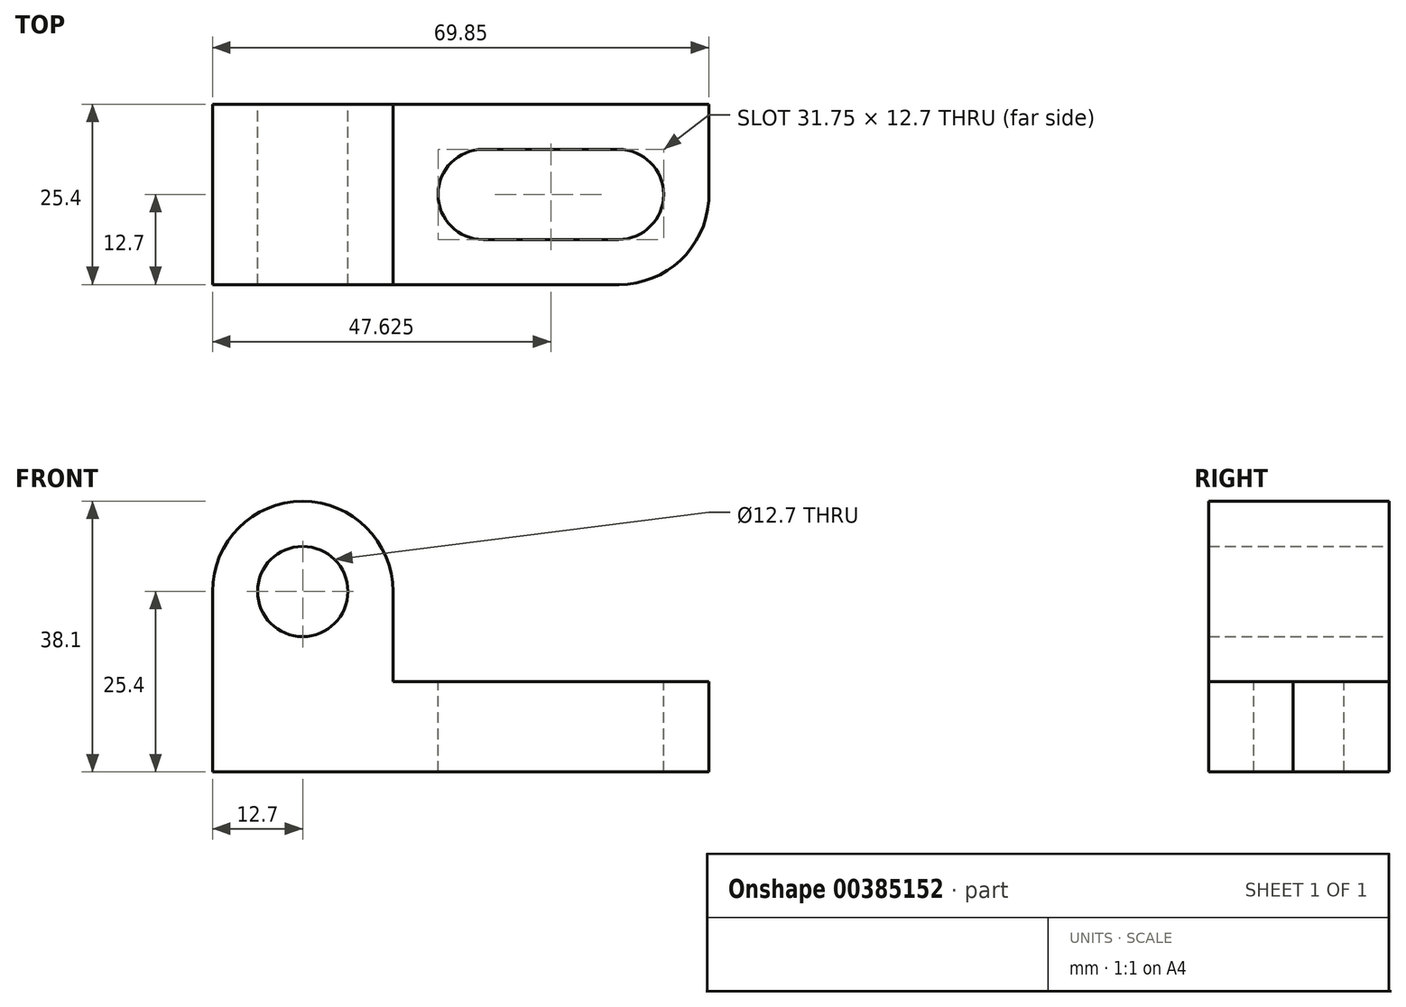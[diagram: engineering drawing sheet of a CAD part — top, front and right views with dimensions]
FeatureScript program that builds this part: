
annotation { "Feature Type Name" : "Feature", "Feature Type Description" : "" }
export const myFeature = defineFeature(function(context is Context, id is Id, definition is map)
    precondition{}
    {
        {
            var Q0;
            Q0=qCreatedBy(makeId("Front.planeOp"),FACE);
            var sketch = newSketch(context, id + "F0", { "sketchPlane" : qUnion([Q0])});
            skLineSegment(sketch, "E0", {"start": v(0, 0) * mm, "end": v(0, 38.1) * mm});
            skLineSegment(sketch, "E1", {"start": v(0, 38.1) * mm, "end": v(25.4, 38.1) * mm});
            skLineSegment(sketch, "E2", {"start": v(25.4, 38.1) * mm, "end": v(25.4, 12.7) * mm});
            skLineSegment(sketch, "E3", {"start": v(25.4, 12.7) * mm, "end": v(69.85, 12.7) * mm});
            skLineSegment(sketch, "E4", {"start": v(69.85, 12.7) * mm, "end": v(69.85, 0) * mm});
            skLineSegment(sketch, "E5", {"start": v(69.85, 0) * mm, "end": v(0, 0) * mm});
            skSolve(sketch);
        }
        {
            var Q0;
            Q0 = qSketchRegion(id + "F0", true);
            extrude(context, id + "F1", {"entities" : qUnion([Q0]), "depth" : 25.4 * mm});
        }
        {
            var Q0;
            Q0=qCreatedBy(makeId("Front.planeOp"),FACE);
            var sketch = newSketch(context, id + "F2", { "sketchPlane" : qUnion([Q0])});
            skCircle(sketch, "E6", {"center": v(12.7, 25.4) * mm, "radius": 6.35 * mm});
            skSolve(sketch);
        }
        {
            var Q0;
            Q0 = qSketchRegion(id + "F2", true);
            extrude(context, id + "F3", {"entities" : qUnion([Q0]), "operationType" : NewBodyOperationType.REMOVE, "depth" : 25.4 * mm});
        }
        {
            var Q0;
            Q0=makeQuery(id+"F1.opExtrude","CAP_FACE",FACE,{"disambiguationData":[OSD([sQuery(id+"F0.wireOp",EDGE,"E0"),sQuery(id+"F0.wireOp",EDGE,"E1"),sQuery(id+"F0.wireOp",EDGE,"E2"),sQuery(id+"F0.wireOp",EDGE,"E3"),sQuery(id+"F0.wireOp",EDGE,"E4"),sQuery(id+"F0.wireOp",EDGE,"E5")])],"isStart":false});
            var sketch = newSketch(context, id + "F4", { "sketchPlane" : qUnion([Q0])});
            skArc(sketch, "E7", {"start": v(25.4, 25.4) * mm, "mid": v(12.7, 38.1) * mm, "end": v(0, 25.4) * mm});
            skSolve(sketch);
        }
        {
            var Q0;
            {var subQ0=sQuery(id+"F4.wireOp",EDGE,"E7");var subQ1=makeQuery(id+"F1.opExtrude","CAP_EDGE",EDGE,{"disambiguationData":[OSD([sQuery(id+"F0.wireOp",EDGE,"E0")])],"isStart":false});var subQ2=makeQuery(id+"F4.imprint","INTERSECT",VERTEX,{"derivedFrom":[subQ1,subQ0]});Q0=makeQuery(id+"F4.imprint","IMPRINT",FACE,{"disambiguationData":[TD([[makeQuery(id+"F4.imprint","IMPRINT",EDGE,{"disambiguationData":[TD([[subQ2,1.0]])],"derivedFrom":subQ0}),-1.0]])]});}
            var Q1;
            {var subQ0=sQuery(id+"F4.wireOp",EDGE,"E7");var subQ1=makeQuery(id+"F1.opExtrude","CAP_EDGE",EDGE,{"disambiguationData":[OSD([sQuery(id+"F0.wireOp",EDGE,"E2")])],"isStart":false});var subQ2=makeQuery(id+"F4.imprint","INTERSECT",VERTEX,{"derivedFrom":[subQ1,subQ0]});Q1=makeQuery(id+"F4.imprint","IMPRINT",FACE,{"disambiguationData":[TD([[makeQuery(id+"F4.imprint","IMPRINT",EDGE,{"disambiguationData":[TD([[subQ2,-1.0]])],"derivedFrom":subQ0}),-1.0]])]});}
            extrude(context, id + "F5", {"entities" : qUnion([Q0, Q1]), "operationType" : NewBodyOperationType.REMOVE, "oppositeDirection" : true, "depth" : 25.4 * mm});
        }
        {
            var Q0;
            Q0=makeQuery(id+"F1.opExtrude","SWEPT_FACE",FACE,{"disambiguationData":[OSD([sQuery(id+"F0.wireOp",EDGE,"E3")])]});
            var sketch = newSketch(context, id + "F6", { "sketchPlane" : qUnion([Q0])});
            skCircle(sketch, "E8", {"center": v(38.1, -12.7) * mm, "radius": 6.35 * mm});
            skCircle(sketch, "E9", {"center": v(57.15, -12.7) * mm, "radius": 6.35 * mm});
            skLineSegment(sketch, "E10", {"start": v(38.1, -6.35) * mm, "end": v(57.15, -6.35) * mm});
            skLineSegment(sketch, "E11", {"start": v(38.1, -19.05) * mm, "end": v(57.15, -19.05) * mm});
            skSolve(sketch);
        }
        {
            var Q0;
            {var subQ0=sQuery(id+"F6.wireOp",EDGE,"E8");var subQ1=makeQuery(id+"F6.imprint","INTERSECT",VERTEX,{"derivedFrom":[subQ0,sQuery(id+"F6.wireOp",EDGE,"E10")]});Q0=makeQuery(id+"F6.imprint","IMPRINT",FACE,{"disambiguationData":[TD([[makeQuery(id+"F6.imprint","IMPRINT",EDGE,{"disambiguationData":[TD([[subQ1,-1.0]])],"derivedFrom":subQ0}),1.0]])]});}
            var Q1;
            {var subQ0=sQuery(id+"F6.wireOp",EDGE,"E10");Q1=makeQuery(id+"F6.imprint","IMPRINT",FACE,{"disambiguationData":[TD([[makeQuery(id+"F6.imprint","IMPRINT",EDGE,{"derivedFrom":subQ0}),-1.0]])]});}
            var Q2;
            {var subQ0=sQuery(id+"F6.wireOp",EDGE,"E9");var subQ1=makeQuery(id+"F6.imprint","INTERSECT",VERTEX,{"derivedFrom":[subQ0,sQuery(id+"F6.wireOp",EDGE,"E10")]});Q2=makeQuery(id+"F6.imprint","IMPRINT",FACE,{"disambiguationData":[TD([[makeQuery(id+"F6.imprint","IMPRINT",EDGE,{"disambiguationData":[TD([[subQ1,-1.0]])],"derivedFrom":subQ0}),1.0]])]});}
            extrude(context, id + "F7", {"entities" : qUnion([Q0, Q1, Q2]), "operationType" : NewBodyOperationType.REMOVE, "oppositeDirection" : true, "depth" : 25.4 * mm});
        }
        {
            var Q0;
            Q0=makeQuery(id+"F1.opExtrude","SWEPT_FACE",FACE,{"disambiguationData":[OSD([sQuery(id+"F0.wireOp",EDGE,"E3")])]});
            var sketch = newSketch(context, id + "F8", { "sketchPlane" : qUnion([Q0])});
            skArc(sketch, "E12", {"start": v(57.15, -25.4) * mm, "mid": v(69.88, -12.7) * mm, "end": v(57.15, 0) * mm});
            skSolve(sketch);
        }
        {
            var Q0;
            {var subQ0=sQuery(id+"F8.wireOp",EDGE,"E12");var subQ1=sQuery(id+"F0.wireOp",EDGE,"E3");var subQ4=makeQuery(id+"F1.opExtrude","SWEPT_EDGE",EDGE,{"disambiguationData":[OSD([subQ1,sQuery(id+"F0.wireOp",EDGE,"E4")])]});var subQ5=makeQuery(id+"F8.imprint","INTERSECT",VERTEX,{"disambiguationData":[OD(1.0)],"derivedFrom":[subQ4,subQ0]});Q0=makeQuery(id+"F8.imprint","IMPRINT",FACE,{"disambiguationData":[TD([[makeQuery(id+"F8.imprint","IMPRINT",EDGE,{"disambiguationData":[TD([[subQ5,-1.0]])],"derivedFrom":subQ0}),-1.0]])]});}
            var Q1;
            {var subQ0=sQuery(id+"F8.wireOp",EDGE,"E12");var subQ1=sQuery(id+"F0.wireOp",EDGE,"E3");var subQ2=makeQuery(id+"F1.opExtrude","CAP_EDGE",EDGE,{"disambiguationData":[OSD([subQ1])],"isStart":false});var subQ3=makeQuery(id+"F8.imprint","INTERSECT",VERTEX,{"derivedFrom":[subQ2,subQ0]});Q1=makeQuery(id+"F8.imprint","IMPRINT",FACE,{"disambiguationData":[TD([[makeQuery(id+"F8.imprint","IMPRINT",EDGE,{"disambiguationData":[TD([[subQ3,-1.0]])],"derivedFrom":subQ0}),-1.0]])]});}
            extrude(context, id + "F9", {"entities" : qUnion([Q0, Q1]), "operationType" : NewBodyOperationType.REMOVE, "oppositeDirection" : true, "depth" : 25.4 * mm});
        }
    });
